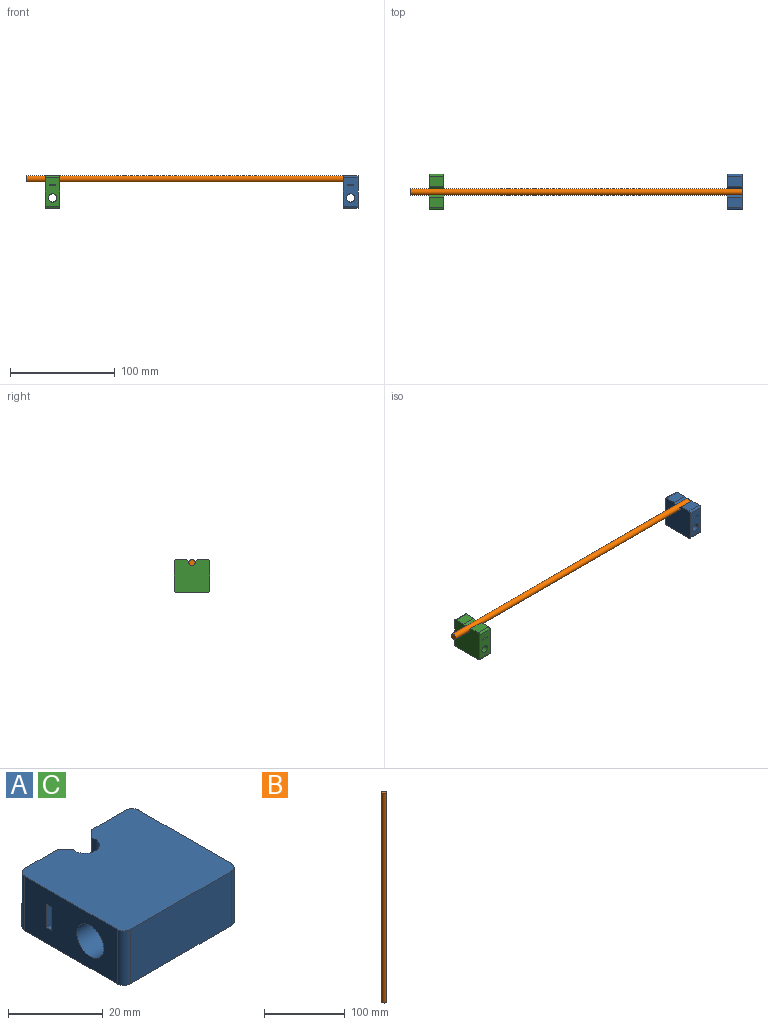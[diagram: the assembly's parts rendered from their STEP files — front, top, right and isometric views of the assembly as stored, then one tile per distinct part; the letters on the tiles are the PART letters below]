
ASSEMBLY  parts=3 mates=1
PART A: 19 faces, bbox 34x31.5x14 mm
  f0: plane 27.5x14mm, normal (1,0,0), area 325.7mm2, adj f3,f7,f10,f11,f12,f13,f14,f15
  f1: plane 27.5x14mm, normal (-1,0,0), area 325.7mm2, adj f3,f7,f10,f11,f12,f13,f14,f16
  f2: plane 14x10mm, normal (0,1,0), area 140mm2, adj f3,f7,f9,f16
  f3: plane 34x31.5mm, normal (0,0,1), area 1031.5mm2, adj f0,f1,f2,f4,f5,f6,f8,f9
  f4: cylinder r=3mm len=14mm, axis (0,0,-1), area 156.7mm2, adj f3,f7,f8,f9
  f5: plane 14x10mm, normal (0,1,0), area 140mm2, adj f3,f7,f8,f15
  f6: plane 30x14mm, normal (0,-1,0), area 420mm2, adj f3,f7,f17,f18
  f7: plane 34x31.5mm, normal (0,0,-1), area 1031.5mm2, adj f0,f1,f2,f4,f5,f6,f8,f9
  f8: plane 14x2.13mm, normal (-0.71,0.71,0), area 42.2mm2, adj f3,f4,f5,f7
  f9: plane 14x2.13mm, normal (0.71,0.71,0), area 42.2mm2, adj f2,f3,f4,f7
  f10: plane 34x6mm, normal (0,-1,0), area 204mm2, adj f0,f1,f11,f13
  f11: plane 34x1.5mm, normal (0,0,-1), area 51mm2, adj f0,f1,f10,f12
  f12: plane 34x6mm, normal (0,1,0), area 204mm2, adj f0,f1,f11,f13
  f13: plane 34x1.5mm, normal (0,0,1), area 51mm2, adj f0,f1,f10,f12
  f14: cylinder r=4mm len=34mm, axis (1,0,0), area 854.5mm2, adj f0,f1
  f15: cylinder r=2mm len=14mm, axis (0,0,1), area 44mm2, adj f0,f3,f5,f7
  f16: cylinder r=2mm len=14mm, axis (0,0,-1), area 44mm2, adj f1,f2,f3,f7
  f17: cylinder r=2mm len=14mm, axis (0,0,1), area 44mm2, adj f1,f3,f6,f7
  f18: cylinder r=2mm len=14mm, axis (0,0,-1), area 44mm2, adj f0,f3,f6,f7
PART B: 3 faces, bbox 6x6x317.5 mm
  f0: cylinder r=3mm len=317.5mm, axis (0,0,-1), area 5984.7mm2, adj f1,f2
  f1: plane 6x6mm, normal (0,0,1), area 28.3mm2, adj f0
  f2: plane 6x6mm, normal (0,0,-1), area 28.3mm2, adj f0
PART C: same geometry as A
PLACE A rot(axis=(0.58,0.58,0.58),120deg) t=(-8.03,108.17,180)mm
PLACE B rot(axis=(0,-1,0),90deg) t=(5.97,108.17,192.75)mm
PLACE C rot(axis=(0.58,0.58,0.58),120deg) t=(-293.03,108.17,180)mm
MATE planar B.f0 <-> A.f4  axis (1,0,0) through (5.97,108.17,192.75)mm
